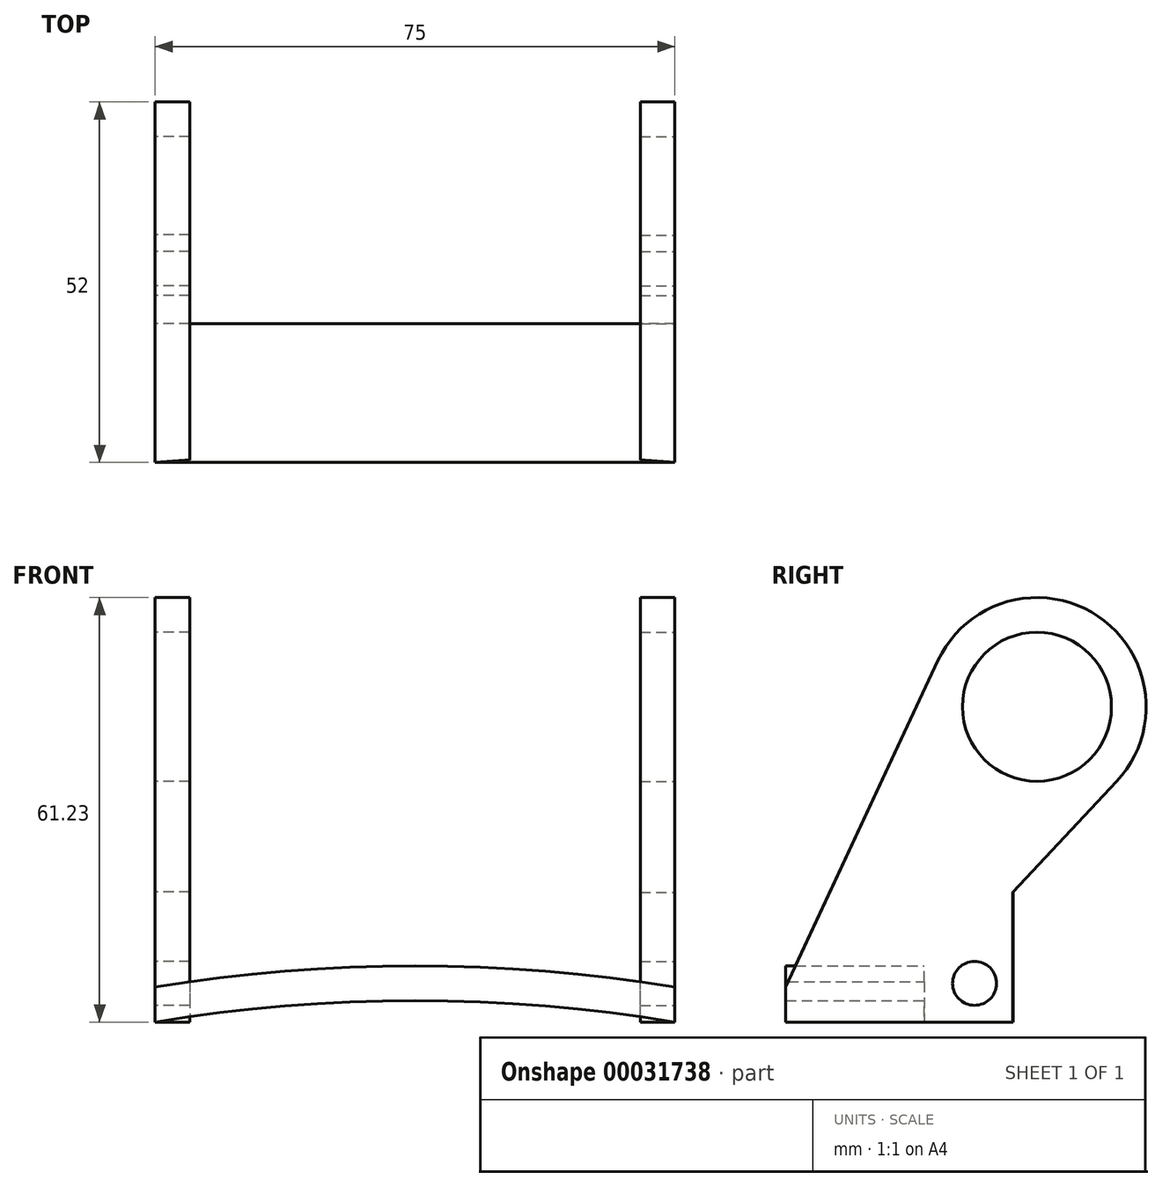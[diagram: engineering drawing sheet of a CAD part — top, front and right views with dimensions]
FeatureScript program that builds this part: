
annotation { "Feature Type Name" : "Feature", "Feature Type Description" : "" }
export const myFeature = defineFeature(function(context is Context, id is Id, definition is map)
    precondition{}
    {
        {
            var Q0;
            Q0=qCreatedBy(makeId("Front.planeOp"),FACE);
            var sketch = newSketch(context, id + "F0", { "sketchPlane" : qUnion([Q0])});
            skLineSegment(sketch, "E0", {"start": v(0, 0) * mm, "end": v(0, 5) * mm, "construction": true});
            skArc(sketch, "E1", {"start": v(37.5, 1.99) * mm, "mid": v(0, 5) * mm, "end": v(-37.5, 1.99) * mm});
            skLineSegment(sketch, "E2", {"start": v(-37.5, 1.99) * mm, "end": v(-37.5, -3.08) * mm});
            skLineSegment(sketch, "E3", {"start": v(37.5, 1.99) * mm, "end": v(37.5, -3.08) * mm});
            skArc(sketch, "E4", {"start": v(37.5, -3.08) * mm, "mid": v(0, 0) * mm, "end": v(-37.5, -3.08) * mm});
            skSolve(sketch);
        }
        {
            var Q0;
            Q0=makeQuery(id+"F0.imprint","IMPRINT",FACE,{"disambiguationData":[TD([[makeQuery(id+"F0.imprint","IMPRINT",EDGE,{"derivedFrom":sQuery(id+"F0.wireOp",EDGE,"E1")}),1.0]])]});
            extrude(context, id + "F1", {"entities" : qUnion([Q0]), "depth" : 20 * mm});
        }
        {
            var Q0;
            Q0=makeQuery(id+"F1.opExtrude","SWEPT_FACE",FACE,{"disambiguationData":[OSD([sQuery(id+"F0.wireOp",EDGE,"E3")])]});
            var sketch = newSketch(context, id + "F2", { "sketchPlane" : qUnion([Q0])});
            skCircle(sketch, "E5", {"center": v(16.25, 42.4) * mm, "radius": 10.75 * mm});
            skArc(sketch, "E6", {"start": v(27.75, 31.64) * mm, "mid": v(25.07, 55.45) * mm, "end": v(1.98, 49.07) * mm});
            skLineSegment(sketch, "E7", {"start": v(-20, 1.99) * mm, "end": v(1.98, 49.07) * mm});
            skLineSegment(sketch, "E8", {"start": v(0, 1.99) * mm, "end": v(27.75, 31.64) * mm});
            skLineSegment(sketch, "E9", {"start": v(-20, 1.99) * mm, "end": v(0, 1.99) * mm});
            skSolve(sketch);
        }
        {
            var Q0;
            Q0=makeQuery(id+"F2.imprint","IMPRINT",FACE,{"disambiguationData":[TD([[makeQuery(id+"F2.imprint","IMPRINT",EDGE,{"derivedFrom":sQuery(id+"F2.wireOp",EDGE,"E5")}),-1.0]])]});
            extrude(context, id + "F3", {"entities" : qUnion([Q0]), "operationType" : NewBodyOperationType.ADD, "oppositeDirection" : true, "depth" : 5 * mm});
        }
        {
            var Q0;
            Q0=makeQuery(id+"F1.opExtrude","SWEPT_FACE",FACE,{"disambiguationData":[OSD([sQuery(id+"F0.wireOp",EDGE,"E2")])]});
            var sketch = newSketch(context, id + "F4", { "sketchPlane" : qUnion([Q0])});
            skCircle(sketch, "E10", {"center": v(-16.25, 42.4) * mm, "radius": 10.75 * mm});
            skArc(sketch, "E11", {"start": v(-1.98, 49.07) * mm, "mid": v(-25.07, 55.45) * mm, "end": v(-27.75, 31.64) * mm});
            skLineSegment(sketch, "E12", {"start": v(0, 1.99) * mm, "end": v(-27.75, 31.64) * mm});
            skLineSegment(sketch, "E13", {"start": v(20, 1.99) * mm, "end": v(-1.98, 49.07) * mm});
            skLineSegment(sketch, "E14", {"start": v(0, 1.99) * mm, "end": v(20, 1.99) * mm});
            skSolve(sketch);
        }
        {
            var Q0;
            Q0 = qSketchRegion(id + "F4", true);
            extrude(context, id + "F5", {"entities" : qUnion([Q0]), "operationType" : NewBodyOperationType.ADD, "oppositeDirection" : true, "depth" : 5 * mm});
        }
        {
            var Q0;
            Q0=makeQuery(id+"F3.boolean.opBoolean","MERGE",FACE,{"derivedFrom":[makeQuery(id+"F1.opExtrude","SWEPT_FACE",FACE,{"disambiguationData":[OSD([sQuery(id+"F0.wireOp",EDGE,"E3")])]}),makeQuery(id+"F3.opExtrude","CAP_FACE",FACE,{"disambiguationData":[OSD([sQuery(id+"F2.wireOp",EDGE,"E5"),sQuery(id+"F2.wireOp",EDGE,"E6"),sQuery(id+"F2.wireOp",EDGE,"E7"),sQuery(id+"F2.wireOp",EDGE,"E8"),sQuery(id+"F2.wireOp",EDGE,"E9")])],"isStart":true})]});
            var sketch = newSketch(context, id + "F6", { "sketchPlane" : qUnion([Q0])});
            skCircle(sketch, "E15", {"center": v(7.24, 2.5) * mm, "radius": 3.18 * mm});
            skLineSegment(sketch, "E16", {"start": v(0, -3.08) * mm, "end": v(12.77, -3.08) * mm});
            skLineSegment(sketch, "E17", {"start": v(12.77, -3.08) * mm, "end": v(12.77, 15.64) * mm});
            skLineSegment(sketch, "E18", {"start": v(12.77, 15.64) * mm, "end": v(0, 1.99) * mm});
            skLineSegment(sketch, "E19", {"start": v(0, 1.99) * mm, "end": v(0, -3.08) * mm});
            skSolve(sketch);
        }
        {
            var Q0;
            Q0=makeQuery(id+"F6.imprint","IMPRINT",FACE,{"disambiguationData":[TD([[makeQuery(id+"F6.imprint","IMPRINT",EDGE,{"derivedFrom":sQuery(id+"F6.wireOp",EDGE,"E15")}),-1.0]])]});
            extrude(context, id + "F7", {"entities" : qUnion([Q0]), "operationType" : NewBodyOperationType.ADD, "oppositeDirection" : true, "depth" : 5 * mm});
        }
        {
            var Q0;
            Q0=makeQuery(id+"F5.boolean.opBoolean","MERGE",FACE,{"derivedFrom":[makeQuery(id+"F1.opExtrude","SWEPT_FACE",FACE,{"disambiguationData":[OSD([sQuery(id+"F0.wireOp",EDGE,"E2")])]}),makeQuery(id+"F5.opExtrude","CAP_FACE",FACE,{"disambiguationData":[OSD([sQuery(id+"F4.wireOp",EDGE,"E10"),sQuery(id+"F4.wireOp",EDGE,"E11"),sQuery(id+"F4.wireOp",EDGE,"E12"),sQuery(id+"F4.wireOp",EDGE,"E13"),sQuery(id+"F4.wireOp",EDGE,"E14")])],"isStart":true})]});
            var sketch = newSketch(context, id + "F8", { "sketchPlane" : qUnion([Q0])});
            skLineSegment(sketch, "E20", {"start": v(0, -3.08) * mm, "end": v(-12.82, -3.08) * mm});
            skLineSegment(sketch, "E21", {"start": v(-12.82, -3.08) * mm, "end": v(-12.82, 15.7) * mm});
            skLineSegment(sketch, "E22", {"start": v(-12.82, 15.7) * mm, "end": v(0, 1.99) * mm});
            skLineSegment(sketch, "E23", {"start": v(0, 1.99) * mm, "end": v(0, -3.08) * mm});
            skCircle(sketch, "E24", {"center": v(-7.24, 2.5) * mm, "radius": 3.17 * mm});
            skSolve(sketch);
        }
        {
            var Q0;
            Q0 = qSketchRegion(id + "F8", true);
            extrude(context, id + "F9", {"entities" : qUnion([Q0]), "operationType" : NewBodyOperationType.ADD, "oppositeDirection" : true, "depth" : 5 * mm});
        }
    });
